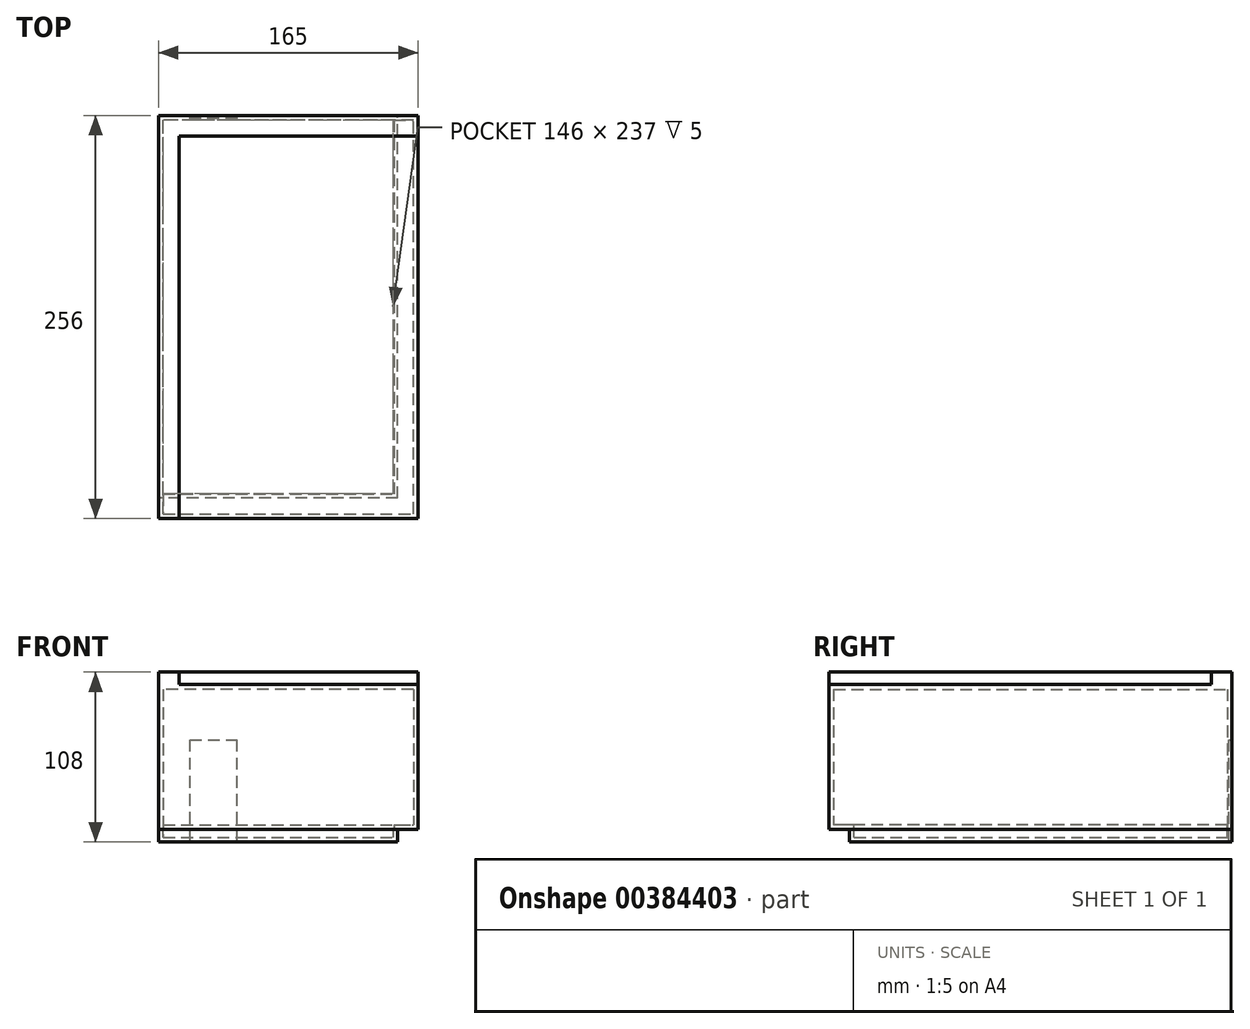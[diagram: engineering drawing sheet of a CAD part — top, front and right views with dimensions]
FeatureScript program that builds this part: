
annotation { "Feature Type Name" : "Feature", "Feature Type Description" : "" }
export const myFeature = defineFeature(function(context is Context, id is Id, definition is map)
    precondition{}
    {
        {
            var Q0;
            Q0=qCreatedBy(makeId("Top.planeOp"),FACE);
            var sketch = newSketch(context, id + "F0", { "sketchPlane" : qUnion([Q0])});
            skLineSegment(sketch, "E0.bottom", {"start": v(82.5, -128) * mm, "end": v(-82.5, -128) * mm});
            skLineSegment(sketch, "E0.top", {"start": v(82.5, 128) * mm, "end": v(-82.5, 128) * mm});
            skLineSegment(sketch, "E0.left", {"start": v(82.5, -128) * mm, "end": v(82.5, 128) * mm});
            skLineSegment(sketch, "E0.right", {"start": v(-82.5, -128) * mm, "end": v(-82.5, 128) * mm});
            skPoint(sketch, "E0.middle", {"position": v(0, 0) * mm});
            skLineSegment(sketch, "E1.0", {"start": v(79.5, 125) * mm, "end": v(-79.5, 125) * mm});
            skLineSegment(sketch, "E1.1", {"start": v(79.5, -125) * mm, "end": v(79.5, 125) * mm});
            skLineSegment(sketch, "E1.2", {"start": v(79.5, -125) * mm, "end": v(-79.5, -125) * mm});
            skLineSegment(sketch, "E1.3", {"start": v(-79.5, -125) * mm, "end": v(-79.5, 125) * mm});
            skSolve(sketch);
        }
        {
            var Q0;
            Q0=makeQuery(id+"F0.imprint","IMPRINT",FACE,{"disambiguationData":[TD([[makeQuery(id+"F0.imprint","IMPRINT",EDGE,{"derivedFrom":sQuery(id+"F0.wireOp",EDGE,"E0.bottom")}),-1.0]])]});
            extrude(context, id + "F1", {"entities" : qUnion([Q0]), "depth" : 100 * mm});
        }
        {
            var Q0;
            Q0=makeQuery(id+"F0.imprint","IMPRINT",FACE,{"disambiguationData":[TD([[makeQuery(id+"F0.imprint","IMPRINT",EDGE,{"derivedFrom":sQuery(id+"F0.wireOp",EDGE,"E0.bottom")}),-1.0]])]});
            var sketch = newSketch(context, id + "F2", { "sketchPlane" : qUnion([Q0])});
            skLineSegment(sketch, "E2.bottom", {"start": v(82.5, 128) * mm, "end": v(-82.5, 128) * mm});
            skLineSegment(sketch, "E2.top", {"start": v(82.5, -128) * mm, "end": v(-82.5, -128) * mm});
            skLineSegment(sketch, "E2.left", {"start": v(82.5, 128) * mm, "end": v(82.5, -128) * mm});
            skLineSegment(sketch, "E2.right", {"start": v(-82.5, 128) * mm, "end": v(-82.5, -128) * mm});
            skPoint(sketch, "E2.middle", {"position": v(0, 0) * mm});
            skSolve(sketch);
        }
        {
            var Q0;
            Q0 = qSketchRegion(id + "F2", true);
            extrude(context, id + "F3", {"entities" : qUnion([Q0]), "operationType" : NewBodyOperationType.ADD, "depth" : 3 * mm});
        }
        {
            var Q0;
            Q0=makeQuery(id+"F1.opExtrude","CAP_FACE",FACE,{"disambiguationData":[OSD([sQuery(id+"F0.wireOp",EDGE,"E0.bottom"),sQuery(id+"F0.wireOp",EDGE,"E0.top"),sQuery(id+"F0.wireOp",EDGE,"E0.left"),sQuery(id+"F0.wireOp",EDGE,"E0.right"),sQuery(id+"F0.wireOp",EDGE,"17e40b48-4ce5-4a4f-af34-9da5c8e43183.0"),sQuery(id+"F0.wireOp",EDGE,"17e40b48-4ce5-4a4f-af34-9da5c8e43183.1"),sQuery(id+"F0.wireOp",EDGE,"17e40b48-4ce5-4a4f-af34-9da5c8e43183.2"),sQuery(id+"F0.wireOp",EDGE,"17e40b48-4ce5-4a4f-af34-9da5c8e43183.3")])],"isStart":false});
            var sketch = newSketch(context, id + "F4", { "sketchPlane" : qUnion([Q0])});
            skLineSegment(sketch, "E3.bottom", {"start": v(82.5, -128) * mm, "end": v(-82.5, -128) * mm});
            skLineSegment(sketch, "E3.top", {"start": v(82.5, 128) * mm, "end": v(-82.5, 128) * mm});
            skLineSegment(sketch, "E3.left", {"start": v(82.5, -128) * mm, "end": v(82.5, 128) * mm});
            skLineSegment(sketch, "E3.right", {"start": v(-82.5, -128) * mm, "end": v(-82.5, 128) * mm});
            skSolve(sketch);
        }
        {
            var Q0;
            Q0 = qSketchRegion(id + "F4", true);
            extrude(context, id + "F5", {"entities" : qUnion([Q0]), "operationType" : NewBodyOperationType.ADD, "oppositeDirection" : true, "depth" : 3 * mm});
        }
        {
            var Q0;
            Q0=makeQuery(id+"F5.boolean.opBoolean","MERGE",FACE,{"derivedFrom":[makeQuery(id+"F1.opExtrude","CAP_FACE",FACE,{"disambiguationData":[OSD([sQuery(id+"F0.wireOp",EDGE,"E0.bottom"),sQuery(id+"F0.wireOp",EDGE,"E0.top"),sQuery(id+"F0.wireOp",EDGE,"E0.left"),sQuery(id+"F0.wireOp",EDGE,"E0.right"),sQuery(id+"F0.wireOp",EDGE,"17e40b48-4ce5-4a4f-af34-9da5c8e43183.0"),sQuery(id+"F0.wireOp",EDGE,"17e40b48-4ce5-4a4f-af34-9da5c8e43183.1"),sQuery(id+"F0.wireOp",EDGE,"17e40b48-4ce5-4a4f-af34-9da5c8e43183.2"),sQuery(id+"F0.wireOp",EDGE,"17e40b48-4ce5-4a4f-af34-9da5c8e43183.3")])],"isStart":false}),makeQuery(id+"F5.opExtrude","CAP_FACE",FACE,{"disambiguationData":[OSD([sQuery(id+"F4.wireOp",EDGE,"E3.bottom"),sQuery(id+"F4.wireOp",EDGE,"E3.top"),sQuery(id+"F4.wireOp",EDGE,"E3.left"),sQuery(id+"F4.wireOp",EDGE,"E3.right")])],"isStart":true})]});
            var sketch = newSketch(context, id + "F6", { "sketchPlane" : qUnion([Q0])});
            skLineSegment(sketch, "E4.bottom", {"start": v(-82.5, -128) * mm, "end": v(-69.5, -128) * mm});
            skLineSegment(sketch, "E4.top", {"start": v(-82.5, 128) * mm, "end": v(-69.5, 128) * mm});
            skLineSegment(sketch, "E4.left", {"start": v(-82.5, -128) * mm, "end": v(-82.5, 128) * mm});
            skLineSegment(sketch, "E4.right", {"start": v(-69.5, -128) * mm, "end": v(-69.5, 115) * mm});
            skLineSegment(sketch, "E5.bottom", {"start": v(82.5, 128) * mm, "end": v(-73.5, 128) * mm});
            skLineSegment(sketch, "E5.top", {"start": v(82.5, 115) * mm, "end": v(-69.5, 115) * mm});
            skLineSegment(sketch, "E5.left", {"start": v(82.5, 128) * mm, "end": v(82.5, 115) * mm});
            skSolve(sketch);
        }
        {
            var Q0;
            Q0 = qSketchRegion(id + "F6", true);
            extrude(context, id + "F7", {"entities" : qUnion([Q0]), "operationType" : NewBodyOperationType.ADD, "depth" : 8 * mm});
        }
        {
            var Q0;
            Q0=qCreatedBy(makeId("Top.planeOp"),FACE);
            var sketch = newSketch(context, id + "F8", { "sketchPlane" : qUnion([Q0])});
            skLineSegment(sketch, "E6.bottom", {"start": v(82.5, -128) * mm, "end": v(-82.5, -128) * mm});
            skLineSegment(sketch, "E6.top", {"start": v(82.5, 128) * mm, "end": v(69.5, 128) * mm});
            skLineSegment(sketch, "E6.left", {"start": v(82.5, -128) * mm, "end": v(82.5, 128) * mm});
            skLineSegment(sketch, "E6.right", {"start": v(-82.5, -128) * mm, "end": v(-82.5, -115) * mm});
            skPoint(sketch, "E6.middle", {"position": v(0, 0) * mm});
            skLineSegment(sketch, "E7.top", {"start": v(69.5, -115) * mm, "end": v(-82.5, -115) * mm});
            skLineSegment(sketch, "E7.left", {"start": v(82.5, -128) * mm, "end": v(82.5, -115) * mm});
            skLineSegment(sketch, "E8.left", {"start": v(82.5, -115) * mm, "end": v(82.5, 128) * mm});
            skLineSegment(sketch, "E8.right", {"start": v(69.5, -115) * mm, "end": v(69.5, 128) * mm});
            skPoint(sketch, "E9.orphan", {"position": v(-82.5, 128) * mm});
            skSolve(sketch);
        }
        {
            var Q0;
            Q0 = qSketchRegion(id + "F8", true);
            extrude(context, id + "F9", {"entities" : qUnion([Q0]), "operationType" : NewBodyOperationType.REMOVE, "depth" : 8 * mm});
        }
        {
            var Q0;
            Q0=makeQuery(id+"F7.boolean.opBoolean","MERGE",FACE,{"derivedFrom":[makeQuery(id+"F1.opExtrude","SWEPT_FACE",FACE,{"disambiguationData":[OSD([sQuery(id+"F0.wireOp",EDGE,"E0.top")])]}),makeQuery(id+"F7.opExtrude","SWEPT_FACE",FACE,{"disambiguationData":[OSD([sQuery(id+"F6.wireOp",EDGE,"E4.top"),sQuery(id+"F6.wireOp",EDGE,"E5.bottom")])]})]});
            var sketch = newSketch(context, id + "F10", { "sketchPlane" : qUnion([Q0])});
            skLineSegment(sketch, "E10.bottom", {"start": v(82.5, 0) * mm, "end": v(62.5, 0) * mm, "construction": true});
            skLineSegment(sketch, "E10.top", {"start": v(82.5, 52.86) * mm, "end": v(62.5, 52.86) * mm, "construction": true});
            skLineSegment(sketch, "E10.left", {"start": v(82.5, 0) * mm, "end": v(82.5, 52.86) * mm, "construction": true});
            skLineSegment(sketch, "E10.right", {"start": v(62.5, 0) * mm, "end": v(62.5, 52.86) * mm, "construction": true});
            skLineSegment(sketch, "E11.bottom", {"start": v(62.5, 0) * mm, "end": v(32.5, 0) * mm});
            skLineSegment(sketch, "E11.top", {"start": v(62.5, 65) * mm, "end": v(32.5, 65) * mm});
            skLineSegment(sketch, "E11.left", {"start": v(62.5, 0) * mm, "end": v(62.5, 65) * mm});
            skLineSegment(sketch, "E11.right", {"start": v(32.5, 0) * mm, "end": v(32.5, 65) * mm});
            skSolve(sketch);
        }
        {
            var Q0;
            Q0 = qSketchRegion(id + "F10", true);
            extrude(context, id + "F11", {"entities" : qUnion([Q0]), "operationType" : NewBodyOperationType.REMOVE, "oppositeDirection" : true, "depth" : 2 * mm});
        }
        {
            var Q0;
            Q0=makeQuery(id+"F9.boolean.opBoolean","COPY",FACE,{"derivedFrom":makeQuery(id+"F9.opExtrude","SWEPT_FACE",FACE,{"disambiguationData":[OSD([sQuery(id+"F8.wireOp",EDGE,"E8.right")])]})});
            var sketch = newSketch(context, id + "F12", { "sketchPlane" : qUnion([Q0])});
            skLineSegment(sketch, "E12.bottom", {"start": v(128, 8) * mm, "end": v(-115, 8) * mm});
            skLineSegment(sketch, "E12.top", {"start": v(128, 0) * mm, "end": v(-115, 0) * mm});
            skLineSegment(sketch, "E12.left", {"start": v(128, 8) * mm, "end": v(128, 0) * mm});
            skLineSegment(sketch, "E12.right", {"start": v(-115, 8) * mm, "end": v(-115, 0) * mm});
            skSolve(sketch);
        }
        {
            var Q0;
            Q0 = qSketchRegion(id + "F12", true);
            extrude(context, id + "F13", {"entities" : qUnion([Q0]), "operationType" : NewBodyOperationType.ADD, "oppositeDirection" : true, "depth" : 3 * mm});
        }
        {
            var Q0;
            Q0=makeQuery(id+"F13.boolean.opBoolean","MERGE",FACE,{"derivedFrom":[makeQuery(id+"F9.boolean.opBoolean","COPY",FACE,{"derivedFrom":makeQuery(id+"F9.opExtrude","SWEPT_FACE",FACE,{"disambiguationData":[OSD([sQuery(id+"F8.wireOp",EDGE,"E7.top")])]})}),makeQuery(id+"F13.opExtrude","SWEPT_FACE",FACE,{"disambiguationData":[OSD([sQuery(id+"F12.wireOp",EDGE,"E12.right")])]})]});
            var sketch = newSketch(context, id + "F14", { "sketchPlane" : qUnion([Q0])});
            skLineSegment(sketch, "E13.bottom", {"start": v(69.5, 8) * mm, "end": v(-82.5, 8) * mm});
            skLineSegment(sketch, "E13.top", {"start": v(69.5, 0) * mm, "end": v(-82.5, 0) * mm});
            skLineSegment(sketch, "E13.left", {"start": v(69.5, 8) * mm, "end": v(69.5, 0) * mm});
            skLineSegment(sketch, "E13.right", {"start": v(-82.5, 8) * mm, "end": v(-82.5, 0) * mm});
            skSolve(sketch);
        }
        {
            var Q0;
            Q0 = qSketchRegion(id + "F14", true);
            extrude(context, id + "F15", {"entities" : qUnion([Q0]), "operationType" : NewBodyOperationType.ADD, "oppositeDirection" : true, "depth" : 3 * mm});
        }
        {
            var Q0;
            Q0=makeQuery(id+"F9.boolean.opBoolean","COPY",FACE,{"derivedFrom":makeQuery(id+"F9.opExtrude","CAP_FACE",FACE,{"disambiguationData":[OSD([sQuery(id+"F8.wireOp",EDGE,"E6.bottom"),sQuery(id+"F8.wireOp",EDGE,"E7.top"),sQuery(id+"F8.wireOp",EDGE,"E7.left"),sQuery(id+"F8.wireOp",EDGE,"E6.right"),sQuery(id+"F8.wireOp",EDGE,"E6.top"),sQuery(id+"F8.wireOp",EDGE,"E8.left"),sQuery(id+"F8.wireOp",EDGE,"E8.right")])],"isStart":false})});
            var sketch = newSketch(context, id + "F16", { "sketchPlane" : qUnion([Q0])});
            skLineSegment(sketch, "E14.bottom", {"start": v(-82.5, 128) * mm, "end": v(82.5, 128) * mm});
            skLineSegment(sketch, "E14.top", {"start": v(-82.5, 112.5) * mm, "end": v(82.5, 112.5) * mm});
            skLineSegment(sketch, "E14.left", {"start": v(-82.5, 128) * mm, "end": v(-82.5, 112.5) * mm});
            skLineSegment(sketch, "E14.right", {"start": v(82.5, 128) * mm, "end": v(82.5, 112.5) * mm});
            skSolve(sketch);
        }
        {
            var Q0;
            Q0 = qSketchRegion(id + "F16", true);
            extrude(context, id + "F17", {"entities" : qUnion([Q0]), "operationType" : NewBodyOperationType.ADD, "oppositeDirection" : true, "depth" : 3 * mm});
        }
        {
            var Q0;
            Q0=makeQuery(id+"F17.boolean.opBoolean","MERGE",FACE,{"derivedFrom":[makeQuery(id+"F9.boolean.opBoolean","COPY",FACE,{"derivedFrom":makeQuery(id+"F9.opExtrude","CAP_FACE",FACE,{"disambiguationData":[OSD([sQuery(id+"F8.wireOp",EDGE,"E6.bottom"),sQuery(id+"F8.wireOp",EDGE,"E7.top"),sQuery(id+"F8.wireOp",EDGE,"E7.left"),sQuery(id+"F8.wireOp",EDGE,"E6.right"),sQuery(id+"F8.wireOp",EDGE,"E6.top"),sQuery(id+"F8.wireOp",EDGE,"E8.left"),sQuery(id+"F8.wireOp",EDGE,"E8.right")])],"isStart":false})}),makeQuery(id+"F17.opExtrude","CAP_FACE",FACE,{"disambiguationData":[OSD([sQuery(id+"F16.wireOp",EDGE,"E14.bottom"),sQuery(id+"F16.wireOp",EDGE,"E14.top"),sQuery(id+"F16.wireOp",EDGE,"E14.left"),sQuery(id+"F16.wireOp",EDGE,"E14.right")])],"isStart":true})]});
            var sketch = newSketch(context, id + "F18", { "sketchPlane" : qUnion([Q0])});
            skLineSegment(sketch, "E15.bottom", {"start": v(82.5, -128) * mm, "end": v(67, -128) * mm});
            skLineSegment(sketch, "E15.top", {"start": v(82.5, 112.5) * mm, "end": v(67, 112.5) * mm});
            skLineSegment(sketch, "E15.left", {"start": v(82.5, -128) * mm, "end": v(82.5, 112.5) * mm});
            skLineSegment(sketch, "E15.right", {"start": v(67, -128) * mm, "end": v(67, 112.5) * mm});
            skSolve(sketch);
        }
        {
            var Q0;
            Q0 = qSketchRegion(id + "F18", true);
            extrude(context, id + "F19", {"entities" : qUnion([Q0]), "operationType" : NewBodyOperationType.ADD, "oppositeDirection" : true, "depth" : 3 * mm});
        }
    });
